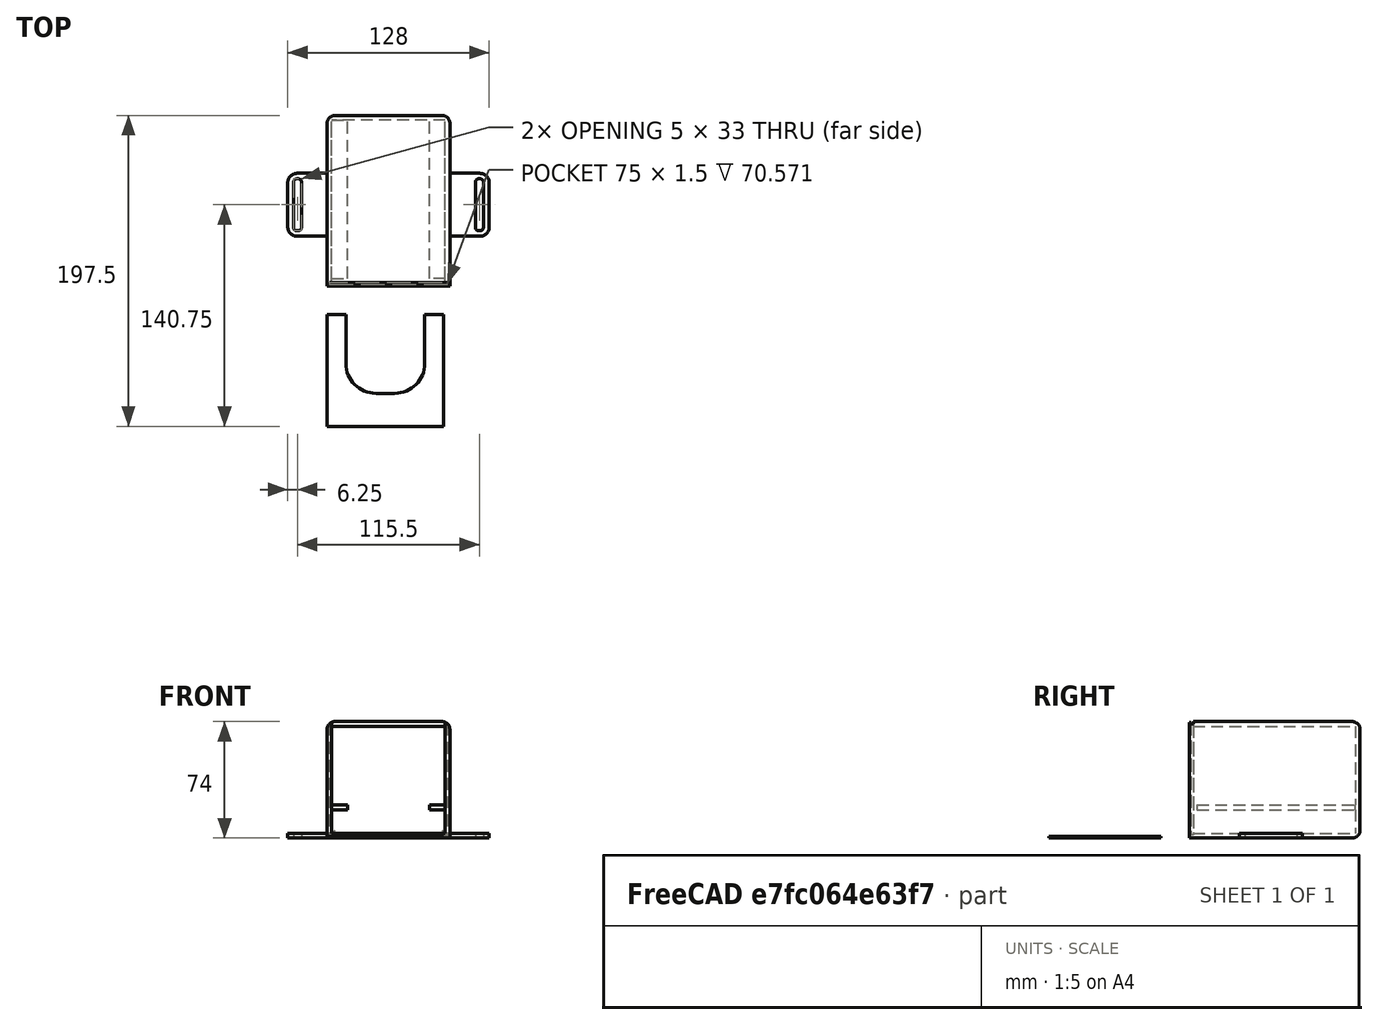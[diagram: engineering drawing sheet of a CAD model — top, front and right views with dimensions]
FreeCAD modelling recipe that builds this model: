
FCSTD DOCUMENT  (FreeCAD 1.0R39319 (Git))
Label: EchoHand_circuit_case
License: All rights reserved
LicenseURL: https://en.wikipedia.org/wiki/All_rights_reserved
objects: Sketcher::SketchObject×17, PartDesign::Pocket×10, PartDesign::Fillet×4, Part::Box×2, PartDesign::FeatureBase×2, App::Link×2, App::FeaturePython×2, PartDesign::Body×2, PartDesign::Pad×2, Assembly::JointGroup×1, Assembly::AssemblyObject×1, PartDesign::Plane×1
note: 91 computed .brp shape members not serialized (recipe doc carries the construction recipe); baked Part::Feature solids carry a one-line shape summary decoded from their .brp

FEATURE [Part::Box] Box  label="Cube"
  AttacherType = Attacher::AttachEngine3D
  Height = 74
  Length = 78
  Width = 108.5
FEATURE [PartDesign::FeatureBase] BaseFeature
  BaseFeature = -> Box
  Suppressed = false
FEATURE [Sketcher::SketchObject] Sketch  label="Board Cutout Sketch"
  ArcFitTolerance = 1e-06
  AttachmentSupport = -> [BaseFeature]
  ExternalGeometry = -> [BaseFeature]
  FullyConstrained = true
  MakeInternals = false
  MapMode = 5
  Placement = pos=(0,0,0) rot=(1,0,0;1.5708rad)
  sketch-geometry (8):
    g0: LineSegment [constr] StartX=0 StartY=74 StartZ=0 EndX=78 EndY=0 EndZ=0
    g1: LineSegment [constr] StartX=0 StartY=0 StartZ=0 EndX=78 EndY=74 EndZ=0
    g2: GeomPoint [constr] X=39 Y=37 Z=0
    g3: LineSegment StartX=3 StartY=21 StartZ=0 EndX=75 EndY=21 EndZ=0
    g4: LineSegment StartX=75 StartY=21 StartZ=0 EndX=75 EndY=71 EndZ=0
    g5: LineSegment StartX=75 StartY=71 StartZ=0 EndX=3 EndY=71 EndZ=0
    g6: LineSegment StartX=3 StartY=71 StartZ=0 EndX=3 EndY=21 EndZ=0
    g7: GeomPoint [constr] X=39 Y=46 Z=0
  constraints (18):
    c: Coincident(g0,g-4)
    c: Coincident(g0,g-6)
    c: Coincident(g1,g-1)
    c: Coincident(g1,g-5)
    c: Symmetric(g0,g0,g2)
    c: Coincident(g3,g4)
    c: Coincident(g4,g5)
    c: Coincident(g5,g6)
    c: Coincident(g6,g3)
    c: Horizontal(g3)
    c: Horizontal(g5)
    c: Vertical(g4)
    c: Vertical(g6)
    c: Symmetric(g5,g3,g7)
    c: Distance(g3,g5) = 50
    c: Vertical(g7,g2)
    c: Distance(g5,g-4) = 3
    c: Distance(g-5,g4) = 3
FEATURE [PartDesign::Pocket] Pocket  label="Board Cutout"
  BaseFeature = -> BaseFeature
  Direction = (0,1,-2e-16)
  Length = 0
  Length2 = 5
  Offset = -3
  Profile = -> Sketch
  ReferenceAxis = -> Sketch [N_Axis]
  Refine = true
  Suppressed = false
  Type = 3
  UpToFace = -> BaseFeature [Face4]
FEATURE [Sketcher::SketchObject] Sketch001  label="Battery Cutout Sketch"
  ArcFitTolerance = 1e-06
  AttachmentSupport = -> [Pocket]
  ExternalGeometry = -> [Pocket]
  FullyConstrained = true
  MakeInternals = false
  MapMode = 5
  Placement = pos=(0,0,0) rot=(1,0,0;1.5708rad)
  sketch-geometry (8):
    g0: LineSegment [constr] StartX=0 StartY=74 StartZ=0 EndX=78 EndY=0 EndZ=0
    g1: LineSegment [constr] StartX=0 StartY=0 StartZ=0 EndX=78 EndY=74 EndZ=0
    g2: GeomPoint [constr] X=39 Y=37 Z=0
    g3: LineSegment StartX=3 StartY=3 StartZ=0 EndX=75 EndY=3 EndZ=0
    g4: LineSegment StartX=75 StartY=3 StartZ=0 EndX=75 EndY=18 EndZ=0
    g5: LineSegment StartX=75 StartY=18 StartZ=0 EndX=3 EndY=18 EndZ=0
    g6: LineSegment StartX=3 StartY=18 StartZ=0 EndX=3 EndY=3 EndZ=0
    g7: GeomPoint [constr] X=39 Y=10.5 Z=0
  constraints (18):
    c: Coincident(g0,g-4)
    c: Coincident(g0,g-6)
    c: Coincident(g1,g-1)
    c: Coincident(g1,g-5)
    c: Symmetric(g1,g1,g2)
    c: Coincident(g3,g4)
    c: Coincident(g4,g5)
    c: Coincident(g5,g6)
    c: Coincident(g6,g3)
    c: Horizontal(g3)
    c: Horizontal(g5)
    c: Vertical(g4)
    c: Vertical(g6)
    c: Symmetric(g5,g3,g7)
    c: Distance(g3,g5) = 15
    c: Vertical(g7,g2)
    c: Distance(g-6,g3) = 3
    c: Distance(g-5,g4) = 3
FEATURE [PartDesign::Pocket] Pocket001  label="Battery Cutout"
  BaseFeature = -> Pocket
  Direction = (0,1,-2e-16)
  Length = 0
  Length2 = 5
  Profile = -> Sketch001
  ReferenceAxis = -> Sketch001 [N_Axis]
  Refine = true
  Suppressed = false
  Type = 3
  UpToFace = -> Pocket [Face11]
FEATURE [Sketcher::SketchObject] Sketch002
  ArcFitTolerance = 1e-06
  AttachmentSupport = -> [Pocket001]
  ExternalGeometry = -> [Pocket001]
  FullyConstrained = true
  MakeInternals = false
  MapMode = 5
  Placement = pos=(0,0,0) rot=(1,0,0;1.5708rad)
  sketch-geometry (6):
    g0: LineSegment [constr] StartX=39 StartY=74 StartZ=0 EndX=39 EndY=0 EndZ=0
    g1: LineSegment StartX=13 StartY=18 StartZ=0 EndX=65 EndY=18 EndZ=0
    g2: LineSegment StartX=65 StartY=18 StartZ=0 EndX=65 EndY=21 EndZ=0
    g3: LineSegment StartX=65 StartY=21 StartZ=0 EndX=13 EndY=21 EndZ=0
    g4: LineSegment StartX=13 StartY=21 StartZ=0 EndX=13 EndY=18 EndZ=0
    g5: GeomPoint [constr] X=39 Y=19.5 Z=0
  constraints (14):
    c: Symmetric(g-3,g-3,g0)
    c: Symmetric(g-6,g-6,g0)
    c: Coincident(g1,g2)
    c: Coincident(g2,g3)
    c: Coincident(g3,g4)
    c: Coincident(g4,g1)
    c: Horizontal(g3)
    c: Vertical(g2)
    c: Vertical(g4)
    c: Symmetric(g3,g1,g5)
    c: PointOnObject(g5,g0)
    c: PointOnObject(g2,g-7)
    c: Tangent(g1,g-8)
    c: DistanceX(g2,g-7) = 10
FEATURE [PartDesign::Pocket] Pocket002  label="Center Cutout"
  BaseFeature = -> Pocket001
  Direction = (0,1,-2e-16)
  Length = 0
  Length2 = 5
  Profile = -> Sketch002
  ReferenceAxis = -> Sketch002 [N_Axis]
  Refine = true
  Suppressed = false
  Type = 3
  UpToFace = -> Pocket001 [Face16]
FEATURE [Sketcher::SketchObject] Sketch008
  ArcFitTolerance = 1e-06
  AttachmentSupport = -> [Pocket002]
  ExternalGeometry = -> [Pocket002]
  FullyConstrained = true
  MakeInternals = false
  MapMode = 5
  Placement = pos=(0,0,74) rot=(0,0,1;0rad)
  sketch-geometry (6):
    g0: LineSegment [constr] StartX=39 StartY=108.5 StartZ=0 EndX=39 EndY=0 EndZ=0
    g1: LineSegment StartX=1.5 StartY=1 StartZ=0 EndX=76.5 EndY=1 EndZ=0
    g2: LineSegment StartX=76.5 StartY=1 StartZ=0 EndX=76.5 EndY=2.5 EndZ=0
    g3: LineSegment StartX=76.5 StartY=2.5 StartZ=0 EndX=1.5 EndY=2.5 EndZ=0
    g4: LineSegment StartX=1.5 StartY=2.5 StartZ=0 EndX=1.5 EndY=1 EndZ=0
    g5: GeomPoint [constr] X=39 Y=1.75 Z=0
  constraints (15):
    c: Symmetric(g-4,g-4,g0)
    c: Symmetric(g-3,g-3,g0)
    c: Coincident(g1,g2)
    c: Coincident(g2,g3)
    c: Coincident(g3,g4)
    c: Coincident(g4,g1)
    c: Horizontal(g1)
    c: Horizontal(g3)
    c: Vertical(g2)
    c: Vertical(g4)
    c: Symmetric(g3,g1,g5)
    c: PointOnObject(g5,g0)
    c: Distance(g-3,g1) = 1
    c: Distance(g1,g3) = 1.5
    c: Distance(g-2,g4) = 1.5
FEATURE [PartDesign::Pocket] Pocket005
  BaseFeature = -> Pocket002
  Direction = (0,0,-1)
  Length = 0
  Length2 = 5
  Offset = 1
  Profile = -> Sketch008
  ReferenceAxis = -> Sketch008 [N_Axis]
  Refine = true
  Suppressed = false
  Type = 3
  UpToFace = -> Pocket002 [Face17]
FEATURE [Sketcher::SketchObject] Sketch009
  ArcFitTolerance = 1e-06
  AttachmentSupport = -> [Pocket005]
  ExternalGeometry = -> [Pocket005]
  FullyConstrained = true
  MakeInternals = false
  MapMode = 5
  Placement = pos=(0,0,0) rot=(1,0,0;1.5708rad)
  sketch-geometry (4):
    g0: LineSegment StartX=13 StartY=18 StartZ=0 EndX=13 EndY=21 EndZ=0
    g1: LineSegment StartX=13 StartY=21 StartZ=0 EndX=3 EndY=21 EndZ=0
    g2: LineSegment StartX=3 StartY=21 StartZ=0 EndX=3 EndY=18 EndZ=0
    g3: LineSegment StartX=3 StartY=18 StartZ=0 EndX=13 EndY=18 EndZ=0
  constraints (10):
    c: Coincident(g0,g1)
    c: Coincident(g1,g2)
    c: Coincident(g2,g3)
    c: Coincident(g3,g0)
    c: Vertical(g0)
    c: Vertical(g2)
    c: Horizontal(g1)
    c: Horizontal(g3)
    c: Coincident(g0,g-3)
    c: Coincident(g1,g-4)
FEATURE [PartDesign::Pocket] Pocket006
  BaseFeature = -> Pocket005
  Direction = (0,1,-2e-16)
  Length = 5
  Length2 = 5
  Profile = -> Sketch009
  ReferenceAxis = -> Sketch009 [N_Axis]
  Refine = true
  Suppressed = false
  Type = 0
FEATURE [Sketcher::SketchObject] Sketch010
  ArcFitTolerance = 1e-06
  AttachmentSupport = -> [Pocket006]
  ExternalGeometry = -> [Pocket006]
  FullyConstrained = true
  MakeInternals = false
  MapMode = 5
  Placement = pos=(0,0,0) rot=(1,0,0;1.5708rad)
  sketch-geometry (4):
    g0: LineSegment StartX=65 StartY=18 StartZ=0 EndX=75 EndY=18 EndZ=0
    g1: LineSegment StartX=75 StartY=18 StartZ=0 EndX=75 EndY=21 EndZ=0
    g2: LineSegment StartX=75 StartY=21 StartZ=0 EndX=65 EndY=21 EndZ=0
    g3: LineSegment StartX=65 StartY=21 StartZ=0 EndX=65 EndY=18 EndZ=0
  constraints (10):
    c: Coincident(g0,g1)
    c: Coincident(g1,g2)
    c: Coincident(g2,g3)
    c: Coincident(g3,g0)
    c: Horizontal(g0)
    c: Horizontal(g2)
    c: Vertical(g1)
    c: Vertical(g3)
    c: Coincident(g0,g-3)
    c: Coincident(g1,g-4)
FEATURE [PartDesign::Pocket] Pocket007
  BaseFeature = -> Pocket006
  Direction = (0,1,-2e-16)
  Length = 5
  Length2 = 5
  Profile = -> Sketch010
  ReferenceAxis = -> Sketch010 [N_Axis]
  Refine = true
  Suppressed = false
  Type = 0
FEATURE [Sketcher::SketchObject] Sketch011
  ArcFitTolerance = 1e-06
  AttachmentSupport = -> [Pocket007]
  ExternalGeometry = -> [Pocket007]
  FullyConstrained = true
  MakeInternals = false
  MapMode = 5
  Placement = pos=(0,0,0) rot=(1,0,0;1.5708rad)
  sketch-geometry (6):
    g0: LineSegment [constr] StartX=3 StartY=71 StartZ=0 EndX=3 EndY=74 EndZ=0
    g1: LineSegment [constr] StartX=75 StartY=71 StartZ=0 EndX=75 EndY=74 EndZ=0
    g2: LineSegment StartX=3 StartY=71 StartZ=0 EndX=75 EndY=71 EndZ=0
    g3: LineSegment StartX=75 StartY=71 StartZ=0 EndX=75 EndY=74 EndZ=0
    g4: LineSegment StartX=75 StartY=74 StartZ=0 EndX=3 EndY=74 EndZ=0
    g5: LineSegment StartX=3 StartY=74 StartZ=0 EndX=3 EndY=71 EndZ=0
  constraints (16):
    c: Coincident(g0,g-3)
    c: PointOnObject(g0,g-4)
    c: Vertical(g0)
    c: Coincident(g1,g-5)
    c: PointOnObject(g1,g-4)
    c: Vertical(g1)
    c: Coincident(g2,g3)
    c: Coincident(g3,g4)
    c: Coincident(g4,g5)
    c: Coincident(g5,g2)
    c: Horizontal(g2)
    c: Horizontal(g4)
    c: Vertical(g3)
    c: Vertical(g5)
    c: Coincident(g2,g0)
    c: Coincident(g3,g1)
FEATURE [PartDesign::Pocket] Pocket008
  BaseFeature = -> Pocket007
  Direction = (0,1,-2e-16)
  Length = 2.5
  Length2 = 5
  Profile = -> Sketch011
  ReferenceAxis = -> Sketch011 [N_Axis]
  Refine = true
  Suppressed = false
  Type = 0
FEATURE [Sketcher::SketchObject] Sketch012
  ArcFitTolerance = 1e-06
  AttachmentSupport = -> [Pocket008]
  ExternalGeometry = -> [Pocket008]
  FullyConstrained = false
  MakeInternals = false
  MapMode = 5
  Placement = pos=(0,0,74) rot=(0,0,1;0rad)
  sketch-geometry (46):
    g0: LineSegment [constr] StartX=0 StartY=108.5 StartZ=0 EndX=78 EndY=108.5 EndZ=0
    g1: LineSegment [constr] StartX=0 StartY=72.3333 StartZ=0 EndX=78 EndY=72.3333 EndZ=0
    g2: LineSegment [constr] StartX=0 StartY=36.1667 StartZ=0 EndX=64.7131 EndY=36.1667 EndZ=0
    g3: LineSegment [constr] StartX=0 StartY=36.1667 StartZ=0 EndX=0 EndY=72.3333 EndZ=0
    g4: LineSegment [constr] StartX=0 StartY=72.3333 StartZ=0 EndX=0 EndY=108.5 EndZ=0
    g5: LineSegment [constr] StartX=0 StartY=0 StartZ=0 EndX=72.7151 EndY=0 EndZ=0
    g6: LineSegment [constr] StartX=0 StartY=0 StartZ=0 EndX=0 EndY=36.1667 EndZ=0
    g7: LineSegment [constr] StartX=39 StartY=108.5 StartZ=0 EndX=39 EndY=0 EndZ=0
    g8: Circle CenterX=39 CenterY=72.3333 CenterZ=0 NormalX=0 NormalY=0 NormalZ=1 AngleXU=0 Radius=25
    g9: LineSegment StartX=36.5 StartY=47.4586 StartZ=0 EndX=41.5 EndY=47.4586 EndZ=0
    g10: LineSegment StartX=41.5 StartY=47.4586 StartZ=0 EndX=41.5 EndY=97.208 EndZ=0
    g11: LineSegment StartX=41.5 StartY=97.208 StartZ=0 EndX=36.5 EndY=97.208 EndZ=0
    g12: LineSegment StartX=36.5 StartY=97.208 StartZ=0 EndX=36.5 EndY=47.4586 EndZ=0
    g13: GeomPoint [constr] X=39 Y=72.3333 Z=0
    g14: LineSegment StartX=41.5 StartY=47.4586 StartZ=0 EndX=46.5 EndY=47.4586 EndZ=0
    g15: LineSegment StartX=46.5 StartY=47.4586 StartZ=0 EndX=46.5 EndY=96.1818 EndZ=0
    g16: LineSegment StartX=46.5 StartY=96.1818 StartZ=0 EndX=41.5 EndY=96.1818 EndZ=0
    g17: LineSegment StartX=41.5 StartY=96.1818 StartZ=0 EndX=41.5 EndY=47.4586 EndZ=0
    g18: LineSegment StartX=46.5 StartY=47.4586 StartZ=0 EndX=51.5 EndY=47.4586 EndZ=0
    g19: LineSegment StartX=51.5 StartY=47.4586 StartZ=0 EndX=51.5 EndY=93.984 EndZ=0
    g20: LineSegment StartX=51.5 StartY=93.984 StartZ=0 EndX=46.5 EndY=93.984 EndZ=0
    g21: LineSegment StartX=46.5 StartY=93.984 StartZ=0 EndX=46.5 EndY=47.4586 EndZ=0
    g22: LineSegment StartX=51.5 StartY=47.4586 StartZ=0 EndX=56.5 EndY=47.4586 EndZ=0
    g23: LineSegment StartX=56.5 StartY=47.4586 StartZ=0 EndX=56.5 EndY=90.1869 EndZ=0
    g24: LineSegment StartX=56.5 StartY=90.1869 StartZ=0 EndX=51.5 EndY=90.1869 EndZ=0
    g25: LineSegment StartX=51.5 StartY=90.1869 StartZ=0 EndX=51.5 EndY=47.4586 EndZ=0
    g26: LineSegment StartX=56.5 StartY=47.4586 StartZ=0 EndX=61.5 EndY=47.4586 EndZ=0
    g27: LineSegment StartX=61.5 StartY=47.4586 StartZ=0 EndX=61.5 EndY=83.2306 EndZ=0
    g28: LineSegment StartX=61.5 StartY=83.2306 StartZ=0 EndX=56.5 EndY=83.2306 EndZ=0
    g29: LineSegment StartX=56.5 StartY=83.2306 StartZ=0 EndX=56.5 EndY=47.4586 EndZ=0
    g30: LineSegment StartX=36.5 StartY=48.0884 StartZ=0 EndX=36.5 EndY=96.1818 EndZ=0
    g31: LineSegment StartX=36.5 StartY=96.1818 StartZ=0 EndX=31.5 EndY=96.1818 EndZ=0
    g32: LineSegment StartX=31.5 StartY=96.1818 StartZ=0 EndX=31.5 EndY=48.0884 EndZ=0
    g33: LineSegment StartX=31.5 StartY=48.0884 StartZ=0 EndX=36.5 EndY=48.0884 EndZ=0
    g34: LineSegment StartX=31.5 StartY=48.0884 StartZ=0 EndX=31.5 EndY=93.984 EndZ=0
    g35: LineSegment StartX=31.5 StartY=93.984 StartZ=0 EndX=26.5 EndY=93.984 EndZ=0
    g36: LineSegment StartX=26.5 StartY=93.984 StartZ=0 EndX=26.5 EndY=48.0884 EndZ=0
    g37: LineSegment StartX=26.5 StartY=48.0884 StartZ=0 EndX=31.5 EndY=48.0884 EndZ=0
    g38: LineSegment StartX=26.5 StartY=48.0884 StartZ=0 EndX=26.5 EndY=90.1869 EndZ=0
    g39: LineSegment StartX=26.5 StartY=90.1869 StartZ=0 EndX=21.5 EndY=90.1869 EndZ=0
    g40: LineSegment StartX=21.5 StartY=90.1869 StartZ=0 EndX=21.5 EndY=48.0884 EndZ=0
    g41: LineSegment StartX=21.5 StartY=48.0884 StartZ=0 EndX=26.5 EndY=48.0884 EndZ=0
    g42: LineSegment StartX=21.5 StartY=48.0884 StartZ=0 EndX=21.5 EndY=83.2306 EndZ=0
    g43: LineSegment StartX=21.5 StartY=83.2306 StartZ=0 EndX=16.5 EndY=83.2306 EndZ=0
    g44: LineSegment StartX=16.5 StartY=83.2306 StartZ=0 EndX=16.5 EndY=48.0884 EndZ=0
    g45: LineSegment StartX=16.5 StartY=48.0884 StartZ=0 EndX=21.5 EndY=48.0884 EndZ=0
  constraints (122):
    c: PointOnObject(g1,g-2)
    c: PointOnObject(g2,g-2)
    c: Coincident(g3,g2)
    c: Coincident(g3,g1)
    c: Coincident(g4,g1)
    c: Coincident(g4,g0)
    c: Coincident(g6,g5)
    c: Coincident(g6,g2)
    c: Coincident(g5,g-1)
    c: Equal(g4,g3)
    c: Equal(g3,g6)
    c: Parallel(g1,g5)
    c: Parallel(g2,g1)
    c: Coincident(g0,g-3)
    c: Equal(g0,g1)
    c: Coincident(g0,g-4)
    c: Horizontal(g1)
    c: Symmetric(g0,g0,g7)
    c: PointOnObject(g7,g5)
    c: Vertical(g7)
    c: Diameter(g8) = 50
    c: Symmetric(g1,g1,g8)
    c: Coincident(g9,g10)
    c: Coincident(g10,g11)
    c: Coincident(g11,g12)
    c: Coincident(g12,g9)
    c: Horizontal(g9)
    c: Horizontal(g11)
    c: Vertical(g10)
    c: Vertical(g12)
    c: Symmetric(g11,g9,g13)
    c: Coincident(g13,g8)
    c: PointOnObject(g10,g8)
    c: Coincident(g14,g15)
    c: Coincident(g15,g16)
    c: Coincident(g16,g17)
    c: Coincident(g17,g14)
    c: Horizontal(g14)
    c: Horizontal(g16)
    c: Vertical(g15)
    c: Vertical(g17)
    c: Coincident(g14,g9)
    c: PointOnObject(g15,g8)
    c: Distance(g10,g12) = 5
    c: Distance(g15,g10) = 5
    c: Coincident(g18,g19)
    c: Coincident(g19,g20)
    c: Coincident(g20,g21)
    c: Coincident(g21,g18)
    c: Horizontal(g18)
    c: Horizontal(g20)
    c: Vertical(g19)
    c: Vertical(g21)
    c: Distance(g19,g21) = 5
    c: Coincident(g18,g14)
    c: PointOnObject(g19,g8)
    c: Coincident(g22,g23)
    c: Coincident(g23,g24)
    c: Coincident(g24,g25)
    c: Coincident(g25,g22)
    c: Horizontal(g22)
    c: Horizontal(g24)
    c: Vertical(g23)
    c: Vertical(g25)
    c: Distance(g23,g25) = 5
    c: Coincident(g22,g18)
    c: PointOnObject(g23,g8)
    c: Coincident(g26,g27)
    c: Coincident(g27,g28)
    c: Coincident(g28,g29)
    c: Coincident(g29,g26)
    c: Horizontal(g26)
    c: Horizontal(g28)
    c: Vertical(g27)
    c: Vertical(g29)
    c: Distance(g27,g29) = 5
    c: Coincident(g26,g22)
    c: PointOnObject(g27,g8)
    c: Coincident(g30,g31)
    c: Coincident(g31,g32)
    c: Coincident(g32,g33)
    c: Coincident(g33,g30)
    c: Vertical(g30)
    c: Vertical(g32)
    c: Horizontal(g31)
    c: Horizontal(g33)
    c: Distance(g30,g32) = 5
    c: PointOnObject(g30,g12)
    c: PointOnObject(g31,g8)
    c: Coincident(g34,g35)
    c: Coincident(g35,g36)
    c: Coincident(g36,g37)
    c: Coincident(g37,g34)
    c: Vertical(g34)
    c: Vertical(g36)
    c: Horizontal(g35)
    c: Horizontal(g37)
    c: Distance(g34,g36) = 5
    c: Coincident(g34,g32)
    c: PointOnObject(g35,g8)
    c: Coincident(g38,g39)
    c: Coincident(g39,g40)
    c: Coincident(g40,g41)
    c: Coincident(g41,g38)
    c: Vertical(g38)
    c: Vertical(g40)
    c: Horizontal(g39)
    c: Horizontal(g41)
    c: Distance(g38,g40) = 5
    c: Coincident(g38,g36)
    c: PointOnObject(g39,g8)
    c: Coincident(g42,g43)
    c: Coincident(g43,g44)
    c: Coincident(g44,g45)
    c: Coincident(g45,g42)
    c: Vertical(g42)
    c: Vertical(g44)
    c: Horizontal(g43)
    c: Horizontal(g45)
    c: Distance(g42,g44) = 5
    c: Coincident(g42,g40)
    c: PointOnObject(g43,g8)
FEATURE [PartDesign::Fillet] Fillet
  Base = -> Pocket008 [Edge12,Edge22,Edge21,Edge3,Edge13,Edge2]
  BaseFeature = -> Pocket008
  Radius = 5
  Refine = true
  SupportTransform = false
  Suppressed = false
  UseAllEdges = false
FEATURE [Sketcher::SketchObject] Sketch013
  ArcFitTolerance = 1e-06
  AttachmentSupport = -> [Fillet]
  ExternalGeometry = -> [Fillet]
  FullyConstrained = true
  MakeInternals = false
  MapMode = 5
  Placement = pos=(0,0,74) rot=(0,0,1;0rad)
  sketch-geometry (1):
    g0: LineSegment [constr] StartX=39 StartY=108.5 StartZ=0 EndX=39 EndY=0 EndZ=0
  constraints (2):
    c: Symmetric(g-4,g-4,g0)
    c: Symmetric(g-5,g-5,g0)
FEATURE [Part::Box] Box001  label="Cube001"
  AttacherType = Attacher::AttachEngine3D
  Height = 1
  Length = 74
  Placement = pos=(2,0,1) rot=(0,0,1;0rad)
  Width = 71
FEATURE [PartDesign::FeatureBase] BaseFeature001
  BaseFeature = -> Box001
  Suppressed = false
FEATURE [App::Link] Carapace  label="Carapace001"
  LinkedObject = -> Body
FEATURE [App::FeaturePython] GroundedJoint  # Assembly grounded joint (typed FeaturePython)
  ObjectToGround = -> Carapace
FEATURE [App::Link] Body002
  LinkPlacement = pos=(76,2.5,77.9634) rot=(0,0.707107,-0.707107;3.14159rad)
  LinkedObject = -> Body001
  Placement = pos=(76,2.5,77.9634) rot=(0,0.707107,-0.707107;3.14159rad)
FEATURE [Sketcher::SketchObject] Sketch014
  ArcFitTolerance = 1e-06
  AttachmentSupport = -> [BaseFeature001]
  FullyConstrained = true
  MakeInternals = false
  MapMode = 5
  Placement = pos=(0,0,1) rot=(0,0,1;0rad)
FEATURE [Sketcher::SketchObject] Sketch015
  ArcFitTolerance = 1e-06
  AttachmentSupport = -> [BaseFeature001]
  FullyConstrained = true
  MakeInternals = false
  MapMode = 5
  Placement = pos=(0,0,1) rot=(0,0,1;0rad)
FEATURE [Sketcher::SketchObject] Sketch016
  ArcFitTolerance = 1e-06
  AttachmentSupport = -> [BaseFeature001]
  ExternalGeometry = -> [BaseFeature001]
  FullyConstrained = true
  MakeInternals = false
  MapMode = 5
  Placement = pos=(0,0,1) rot=(0,0,1;0rad)
  sketch-geometry (8):
    g0: LineSegment [constr] StartX=0 StartY=71 StartZ=0 EndX=74 EndY=0 EndZ=0
    g1: LineSegment [constr] StartX=0 StartY=0 StartZ=0 EndX=74 EndY=71 EndZ=0
    g2: GeomPoint [constr] X=37 Y=35.5 Z=0
    g3: LineSegment StartX=12 StartY=21 StartZ=0 EndX=62 EndY=21 EndZ=0
    g4: LineSegment StartX=62 StartY=21 StartZ=0 EndX=62 EndY=71 EndZ=0
    g5: LineSegment StartX=62 StartY=71 StartZ=0 EndX=12 EndY=71 EndZ=0
    g6: LineSegment StartX=12 StartY=71 StartZ=0 EndX=12 EndY=21 EndZ=0
    g7: GeomPoint [constr] X=37 Y=46 Z=0
  constraints (17):
    c: Coincident(g0,g-5)
    c: Coincident(g0,g-6)
    c: Coincident(g1,g-1)
    c: Coincident(g1,g-6)
    c: Symmetric(g1,g1,g2)
    c: Coincident(g3,g4)
    c: Coincident(g4,g5)
    c: Coincident(g5,g6)
    c: Coincident(g6,g3)
    c: Horizontal(g3)
    c: Vertical(g4)
    c: Vertical(g6)
    c: Symmetric(g5,g3,g7)
    c: Distance(g4,g6) = 50
    c: Distance(g3,g5) = 50
    c: Tangent(g5,g-3)
    c: Vertical(g7,g2)
FEATURE [PartDesign::Pocket] Pocket009
  BaseFeature = -> BaseFeature001
  Direction = (0,0,-1)
  Length = 5
  Length2 = 5
  Profile = -> Sketch016
  ReferenceAxis = -> Sketch016 [N_Axis]
  Refine = true
  Suppressed = false
  Type = 1
FEATURE [PartDesign::Fillet] Fillet001
  Base = -> Pocket009 [Edge22,Edge23]
  BaseFeature = -> Pocket009
  Placement = pos=(0,5,0) rot=(0,0,1;0rad)
  Radius = 19
  Refine = true
  SupportTransform = false
  Suppressed = false
  UseAllEdges = false
FEATURE [PartDesign::Body] Body001  label="Lid"
  AllowCompound = false
  BaseFeature = -> Box001
  Group = -> [BaseFeature001,Sketch014,Sketch015,Sketch016,Pocket009,Fillet001]
  Origin = -> Origin001
  Placement = pos=(0,-89,0) rot=(0,0,1;0rad)
  Tip = -> Fillet001
FEATURE [App::FeaturePython] Joint  label="Parallel"  # Assembly joint (typed FeaturePython)
  Activated = true
  AngleMax = 0
  AngleMin = 0
  Detach1 = false
  Detach2 = false
  Distance = 0
  Distance2 = 0
  EnableAngleMax = false
  EnableAngleMin = false
  EnableLengthMax = false
  EnableLengthMin = false
  JointType = 6 (Parallel)
  LengthMax = 0
  LengthMin = 0
  Placement1 = pos=(37,25.9298,0) rot=(0,0,1;0rad)
  Placement2 = pos=(87.5,71.75,1.5) rot=(0.57735,-0.57735,0.57735;2.0944rad)
  Reference1 = -> Assembly [Body002.Face12,Body002.Face12]
  Reference2 = -> Assembly [Carapace.Face15,Carapace.Face15]
FEATURE [Assembly::JointGroup] Joints
  Group = -> [GroundedJoint,Joint]
FEATURE [Assembly::AssemblyObject] Assembly
  Group = -> [Joints,Carapace,GroundedJoint,Body002,Joint]
  Origin = -> Origin002
  Type = Assembly
FEATURE [Sketcher::SketchObject] Sketch017
  ArcFitTolerance = 1e-06
  AttachmentSupport = -> [Fillet]
  FullyConstrained = true
  MakeInternals = false
  MapMode = 5
  Placement = pos=(0,0,0) rot=(1,0,0;3.14159rad)
  sketch-geometry (8):
    g0: LineSegment StartX=73 StartY=-72 StartZ=0 EndX=98 EndY=-72 EndZ=0
    g1: LineSegment StartX=98 StartY=-72 StartZ=0 EndX=98 EndY=-32 EndZ=0
    g2: LineSegment StartX=98 StartY=-32 StartZ=0 EndX=73 EndY=-32 EndZ=0
    g3: LineSegment StartX=73 StartY=-32 StartZ=0 EndX=73 EndY=-72 EndZ=0
    g4: LineSegment [constr] StartX=73 StartY=-32 StartZ=0 EndX=98 EndY=-72 EndZ=0
    g5: LineSegment [constr] StartX=73 StartY=-72 StartZ=0 EndX=98 EndY=-32 EndZ=0
    g6: GeomPoint [constr] X=85.5 Y=-52 Z=0
    g7: LineSegment [constr] StartX=85.5 StartY=-52 StartZ=0 EndX=98 EndY=-52 EndZ=0
  constraints (18):
    c: Coincident(g0,g1)
    c: Coincident(g1,g2)
    c: Coincident(g2,g3)
    c: Coincident(g3,g0)
    c: Horizontal(g0)
    c: Horizontal(g2)
    c: Vertical(g1)
    c: Tangent(g3,g-3)
    c: Distance(g1,g3) = 25
    c: Distance(g0,g2) = 40
    c: Coincident(g4,g2)
    c: Coincident(g4,g0)
    c: Coincident(g5,g0)
    c: Coincident(g5,g1)
    c: Symmetric(g4,g4,g6)
    c: Coincident(g7,g6)
    c: Symmetric(g1,g1,g7)
    c: Distance(g-4,g7) = 51.5
FEATURE [PartDesign::Plane] DatumPlane
  Length = 154.144
  MapMode = 5
  Placement = pos=(0,0,-2e-16) rot=(1,0,0;3.14159rad)
  ResizeMode = 0
  Width = 159.644
FEATURE [Sketcher::SketchObject] Sketch018
  ArcFitTolerance = 1e-06
  AttachmentSupport = -> [Fillet]
  ExternalGeometry = -> [Fillet,DatumPlane]
  FullyConstrained = false
  MakeInternals = false
  MapMode = 5
  Placement = pos=(78,0,0) rot=(0.57735,0.57735,0.57735;2.0944rad)
  sketch-geometry (13):
    g0: LineSegment StartX=31.75 StartY=3 StartZ=0 EndX=31.75 EndY=0 EndZ=0
    g1: LineSegment StartX=31.75 StartY=-2e-16 StartZ=0 EndX=71.75 EndY=-2e-16 EndZ=0
    g2: LineSegment StartX=71.75 StartY=-2e-16 StartZ=0 EndX=71.75 EndY=3 EndZ=0
    g3: LineSegment StartX=71.75 StartY=3 StartZ=0 EndX=31.75 EndY=3 EndZ=0
    g4: LineSegment [constr] StartX=31.75 StartY=3 StartZ=0 EndX=71.75 EndY=0 EndZ=0
    g5: LineSegment [constr] StartX=31.75 StartY=-2e-16 StartZ=0 EndX=71.75 EndY=3 EndZ=0
    g6: GeomPoint [constr] X=51.75 Y=1.5 Z=0
    g7: LineSegment [constr] StartX=108.5 StartY=5 StartZ=0 EndX=108.5 EndY=-5.12074 EndZ=0
    g8: LineSegment [constr] StartX=103.5 StartY=0 StartZ=0 EndX=123.61 EndY=0 EndZ=0
    g9: GeomPoint [constr] X=108.5 Y=-0.060368 Z=0
    g10: LineSegment [constr] StartX=0 StartY=69 StartZ=0 EndX=103.5 EndY=0 EndZ=0
    g11: LineSegment [constr] StartX=0 StartY=0 StartZ=0 EndX=103.5 EndY=69 EndZ=0
    g12: GeomPoint [constr] X=51.75 Y=34.5 Z=0
  constraints (26):
    c: Coincident(g0,g1)
    c: Coincident(g1,g2)
    c: Coincident(g2,g3)
    c: Coincident(g3,g0)
    c: Vertical(g0)
    c: Vertical(g2)
    c: Horizontal(g3)
    c: Distance(g0,g2) = 40
    c: Distance(g1,g3) = 3
    c: Coincident(g4,g0)
    c: Coincident(g4,g1)
    c: Coincident(g5,g0)
    c: Coincident(g5,g2)
    c: Symmetric(g4,g4,g6)
    c: Coincident(g7,g-3)
    c: Vertical(g7)
    c: Coincident(g8,g-9)
    c: Horizontal(g8)
    c: Symmetric(g7,g7,g9)
    c: Coincident(g10,g-4)
    c: Coincident(g10,g8)
    c: Coincident(g11,g-1)
    c: Coincident(g11,g-9)
    c: Symmetric(g11,g11,g12)
    c: Vertical(g6,g12)
    c: Tangent(g1,g-6)
FEATURE [PartDesign::Pad] Pad
  BaseFeature = -> Fillet
  Direction = (1,0,0)
  Length = 25
  Length2 = 10
  Profile = -> Sketch018
  ReferenceAxis = -> Sketch018 [N_Axis]
  Refine = true
  Suppressed = false
  Type = 0
FEATURE [Sketcher::SketchObject] Sketch019
  ArcFitTolerance = 1e-06
  AttachmentSupport = -> [Pad]
  ExternalGeometry = -> [Pad,DatumPlane]
  FullyConstrained = true
  MakeInternals = false
  MapMode = 5
  Placement = pos=(0,0,0) rot=(0.57735,-0.57735,-0.57735;2.0944rad)
  sketch-geometry (8):
    g0: LineSegment [constr] StartX=-103.5 StartY=69 StartZ=0 EndX=0 EndY=0 EndZ=0
    g1: LineSegment [constr] StartX=-103.5 StartY=0 StartZ=0 EndX=0 EndY=69 EndZ=0
    g2: GeomPoint [constr] X=-51.75 Y=34.5 Z=0
    g3: LineSegment StartX=-71.75 StartY=-2e-16 StartZ=0 EndX=-31.75 EndY=-2e-16 EndZ=0
    g4: LineSegment StartX=-31.75 StartY=-2e-16 StartZ=0 EndX=-31.75 EndY=3 EndZ=0
    g5: LineSegment StartX=-31.75 StartY=3 StartZ=0 EndX=-71.75 EndY=3 EndZ=0
    g6: LineSegment StartX=-71.75 StartY=3 StartZ=0 EndX=-71.75 EndY=0 EndZ=0
    g7: GeomPoint [constr] X=-51.75 Y=1.5 Z=0
  constraints (17):
    c: Coincident(g0,g-5)
    c: Coincident(g0,g-1)
    c: Coincident(g1,g-3)
    c: Coincident(g1,g-5)
    c: Symmetric(g0,g0,g2)
    c: Coincident(g3,g4)
    c: Coincident(g4,g5)
    c: Coincident(g5,g6)
    c: Coincident(g6,g3)
    c: Horizontal(g5)
    c: Vertical(g4)
    c: Vertical(g6)
    c: Symmetric(g5,g3,g7)
    c: Distance(g4,g6) = 40
    c: Distance(g3,g5) = 3
    c: Vertical(g7,g2)
    c: Tangent(g3,g-4)
FEATURE [PartDesign::Pad] Pad001
  BaseFeature = -> Pad
  Direction = (-1,0,0)
  Length = 25
  Length2 = 10
  Profile = -> Sketch019
  ReferenceAxis = -> Sketch019 [N_Axis]
  Refine = true
  Suppressed = false
  Type = 0
FEATURE [Sketcher::SketchObject] Sketch020
  ArcFitTolerance = 1e-06
  AttachmentSupport = -> [Pad001]
  ExternalGeometry = -> [Pad001]
  FullyConstrained = true
  MakeInternals = false
  MapMode = 5
  Placement = pos=(0,0,3) rot=(0,0,1;0rad)
  sketch-geometry (9):
    g0: LineSegment [constr] StartX=78 StartY=71.75 StartZ=0 EndX=103 EndY=31.75 EndZ=0
    g1: LineSegment [constr] StartX=78 StartY=31.75 StartZ=0 EndX=103 EndY=71.75 EndZ=0
    g2: GeomPoint [constr] X=90.5 Y=51.75 Z=0
    g3: LineSegment StartX=94.25 StartY=35.25 StartZ=0 EndX=99.25 EndY=35.25 EndZ=0
    g4: LineSegment StartX=99.25 StartY=35.25 StartZ=0 EndX=99.25 EndY=68.25 EndZ=0
    g5: LineSegment StartX=99.25 StartY=68.25 StartZ=0 EndX=94.25 EndY=68.25 EndZ=0
    g6: LineSegment StartX=94.25 StartY=68.25 StartZ=0 EndX=94.25 EndY=35.25 EndZ=0
    g7: GeomPoint [constr] X=96.75 Y=51.75 Z=0
    g8: GeomPoint X=103 Y=51.75 Z=0
  constraints (18):
    c: Coincident(g0,g-3)
    c: Coincident(g0,g-6)
    c: Coincident(g1,g-6)
    c: Coincident(g1,g-5)
    c: Symmetric(g1,g1,g2)
    c: Coincident(g3,g4)
    c: Coincident(g4,g5)
    c: Coincident(g5,g6)
    c: Coincident(g6,g3)
    c: Horizontal(g3)
    c: Horizontal(g5)
    c: Vertical(g4)
    c: Vertical(g6)
    c: Symmetric(g5,g3,g7)
    c: Distance(g4,g6) = 5
    c: Distance(g3,g5) = 33
    c: Symmetric(g-5,g-5,g8)
    c: Symmetric(g2,g8,g7)
FEATURE [PartDesign::Pocket] Pocket010
  BaseFeature = -> Pad001
  Direction = (0,0,-1)
  Length = 5
  Length2 = 5
  Profile = -> Sketch020
  ReferenceAxis = -> Sketch020 [N_Axis]
  Refine = true
  Suppressed = false
  Type = 1
FEATURE [Sketcher::SketchObject] Sketch021
  ArcFitTolerance = 1e-06
  AttachmentSupport = -> [Pocket010]
  ExternalGeometry = -> [Pocket010]
  FullyConstrained = true
  MakeInternals = false
  MapMode = 5
  Placement = pos=(0,0,3) rot=(0,0,1;0rad)
  sketch-geometry (9):
    g0: LineSegment [constr] StartX=-25 StartY=71.75 StartZ=0 EndX=0 EndY=31.75 EndZ=0
    g1: LineSegment [constr] StartX=-25 StartY=31.75 StartZ=0 EndX=0 EndY=71.75 EndZ=0
    g2: GeomPoint [constr] X=-12.5 Y=51.75 Z=0
    g3: LineSegment StartX=-21.25 StartY=35.25 StartZ=0 EndX=-16.25 EndY=35.25 EndZ=0
    g4: LineSegment StartX=-16.25 StartY=35.25 StartZ=0 EndX=-16.25 EndY=68.25 EndZ=0
    g5: LineSegment StartX=-16.25 StartY=68.25 StartZ=0 EndX=-21.25 EndY=68.25 EndZ=0
    g6: LineSegment StartX=-21.25 StartY=68.25 StartZ=0 EndX=-21.25 EndY=35.25 EndZ=0
    g7: GeomPoint [constr] X=-18.75 Y=51.75 Z=0
    g8: GeomPoint [constr] X=-25 Y=51.75 Z=0
  constraints (18):
    c: Coincident(g0,g-4)
    c: Coincident(g0,g-6)
    c: Coincident(g1,g-6)
    c: Coincident(g1,g-4)
    c: Symmetric(g1,g1,g2)
    c: Coincident(g3,g4)
    c: Coincident(g4,g5)
    c: Coincident(g5,g6)
    c: Coincident(g6,g3)
    c: Horizontal(g3)
    c: Horizontal(g5)
    c: Vertical(g4)
    c: Vertical(g6)
    c: Symmetric(g5,g3,g7)
    c: Distance(g4,g6) = 5
    c: Distance(g3,g5) = 33
    c: Symmetric(g-3,g-3,g8)
    c: Symmetric(g8,g2,g7)
FEATURE [PartDesign::Pocket] Pocket011
  BaseFeature = -> Pocket010
  Direction = (0,0,-1)
  Length = 5
  Length2 = 5
  Profile = -> Sketch021
  ReferenceAxis = -> Sketch021 [N_Axis]
  Refine = true
  Suppressed = false
  Type = 1
FEATURE [PartDesign::Fillet] Fillet002
  Base = -> Pocket011 [Edge95,Edge92,Edge93,Edge97,Edge89,Edge90,Edge87,Edge88]
  BaseFeature = -> Pocket011
  Radius = 2
  Refine = true
  SupportTransform = false
  Suppressed = false
  UseAllEdges = false
FEATURE [PartDesign::Fillet] Fillet003
  Base = -> Fillet002 [Edge69,Edge67,Edge65,Edge58]
  BaseFeature = -> Fillet002
  Radius = 6
  Refine = true
  SupportTransform = false
  Suppressed = false
  UseAllEdges = false
FEATURE [PartDesign::Body] Body  label="Case"
  AllowCompound = false
  BaseFeature = -> Box
  Group = -> [BaseFeature,Sketch,Pocket,Sketch001,Pocket001,Sketch002,Pocket002,Sketch008,Pocket005,Sketch009,Pocket006,Sketch010,Pocket007,Sketch011,Pocket008,Sketch012,Fillet,Sketch013,Sketch017,DatumPlane,Sketch018,Pad,Sketch019,Pad001,Sketch020,Pocket010,Sketch021,Pocket011,Fillet002,Fillet003]
  Origin = -> Origin
  Tip = -> Fillet003
